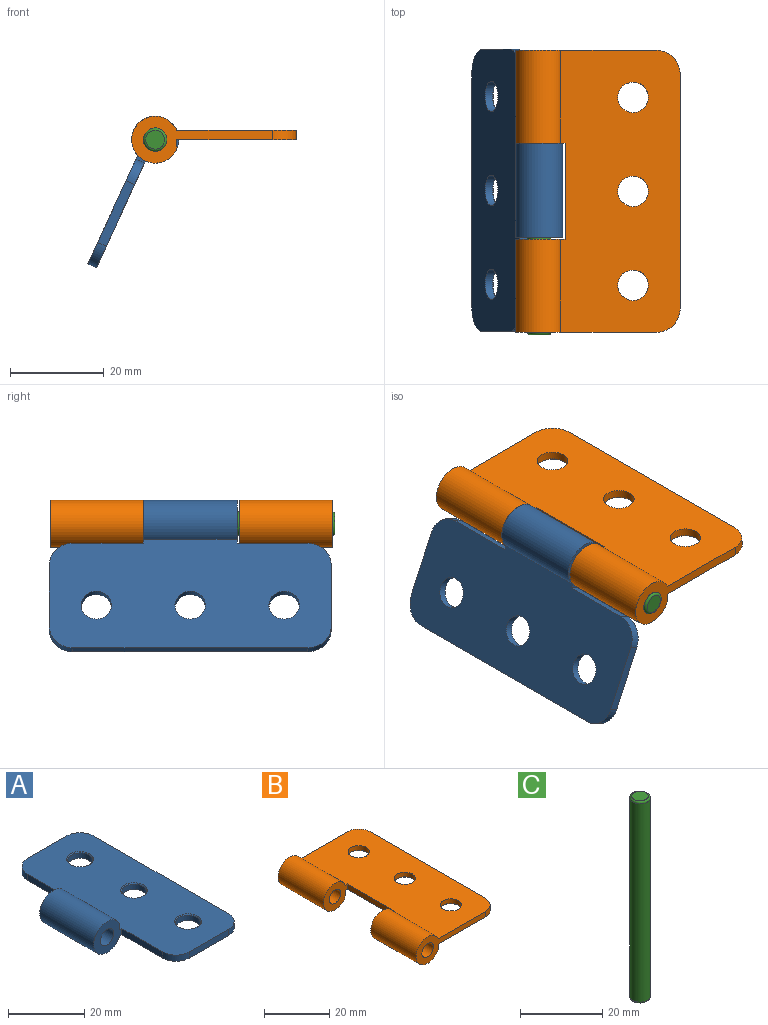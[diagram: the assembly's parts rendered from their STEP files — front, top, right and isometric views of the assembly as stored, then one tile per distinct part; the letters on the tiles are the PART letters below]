
ASSEMBLY  parts=3 mates=4
PART A: 22 faces, bbox 35x60x10 mm
  f0: cone r=3.5mm half-angle=45deg, axis (0,0,1), area 7.5mm2, adj f1,f10
  f1: cylinder r=3.25mm len=6.5mm, axis (0,0,1), area 35.7mm2, adj f0,f12
  f2: cone r=3.5mm half-angle=45deg, axis (0,0,1), area 7.5mm2, adj f3,f10
  f3: cylinder r=3.25mm len=6.5mm, axis (0,0,1), area 35.7mm2, adj f2,f12
  f4: cone r=3.5mm half-angle=45deg, axis (0,0,1), area 7.5mm2, adj f5,f10
  f5: cylinder r=3.25mm len=6.5mm, axis (0,0,1), area 35.7mm2, adj f4,f12
  f6: cylinder r=2.5mm len=20mm, axis (0,-1,0), area 314.2mm2, adj f16,f17
  f7: cylinder r=5mm len=20mm, axis (0,-1,0), area 546mm2, adj f12,f15,f16,f17
  f8: plane 15x2mm, normal (-1,0,0), area 30mm2, adj f10,f12,f17,f20
  f9: plane 15x2mm, normal (-1,0,0), area 30mm2, adj f10,f12,f16,f21
  f10: plane 60x25.42mm, normal (0,0,1), area 1351.4mm2, adj f0,f2,f4,f8,f9,f11,f13,f14
  f11: plane 50x2mm, normal (1,0,0), area 100mm2, adj f10,f12,f18,f19
  f12: plane 60x25.42mm, normal (0,0,-1), area 1367.3mm2, adj f1,f3,f5,f7,f8,f9,f11,f13
  f13: plane 14.5x2mm, normal (0,1,0), area 29mm2, adj f10,f12,f18,f21
  f14: plane 14.5x2mm, normal (0,-1,0), area 29mm2, adj f10,f12,f19,f20
  f15: plane 20x2mm, normal (1,0,0), area 40mm2, adj f7,f10,f16,f17
  f16: plane 10.5x10mm, normal (0,1,0), area 59.6mm2, adj f6,f7,f9,f10,f12,f15
  f17: plane 10.5x10mm, normal (0,-1,0), area 59.6mm2, adj f6,f7,f8,f10,f12,f15
  f18: cylinder r=5mm len=5mm, axis (0,0,1), area 15.7mm2, adj f10,f11,f12,f13
  f19: cylinder r=5mm len=5mm, axis (0,0,-1), area 15.7mm2, adj f10,f11,f12,f14
  f20: cylinder r=5mm len=5mm, axis (0,0,1), area 15.7mm2, adj f8,f10,f12,f14
  f21: cylinder r=5mm len=5mm, axis (0,0,-1), area 15.7mm2, adj f9,f10,f12,f13
PART B: 22 faces, bbox 35x60x10 mm
  f0: cone r=3.5mm half-angle=45deg, axis (0,0,-1), area 7.5mm2, adj f1,f10
  f1: cylinder r=3.25mm len=6.5mm, axis (0,0,-1), area 35.7mm2, adj f0,f12
  f2: cone r=3.5mm half-angle=45deg, axis (0,0,-1), area 7.5mm2, adj f3,f10
  f3: cylinder r=3.25mm len=6.5mm, axis (0,0,-1), area 35.7mm2, adj f2,f12
  f4: cone r=3.5mm half-angle=45deg, axis (0,0,-1), area 7.5mm2, adj f5,f10
  f5: cylinder r=3.25mm len=6.5mm, axis (0,0,-1), area 35.7mm2, adj f4,f12
  f6: cylinder r=2.5mm len=19.75mm, axis (0,-1,0), area 310.2mm2, adj f15,f19
  f7: cylinder r=5mm len=19.75mm, axis (0,-1,0), area 539.2mm2, adj f12,f13,f15,f19
  f8: cylinder r=2.5mm len=19.75mm, axis (0,-1,0), area 310.2mm2, adj f16,f18
  f9: cylinder r=5mm len=19.75mm, axis (0,-1,0), area 539.2mm2, adj f11,f12,f16,f18
  f10: plane 60x25.42mm, normal (0,0,-1), area 1380.1mm2, adj f0,f2,f4,f11,f13,f14,f15,f16
  f11: plane 19.75x2mm, normal (1,0,0), area 39.5mm2, adj f9,f10,f16,f18
  f12: plane 60x25.42mm, normal (0,0,1), area 1396mm2, adj f1,f3,f5,f7,f9,f14,f15,f16
  f13: plane 19.75x2mm, normal (1,0,0), area 39.5mm2, adj f7,f10,f15,f19
  f14: plane 50x2mm, normal (1,0,0), area 100mm2, adj f10,f12,f20,f21
  f15: plane 30x10mm, normal (0,1,0), area 98.6mm2, adj f6,f7,f10,f12,f13,f20
  f16: plane 30x10mm, normal (0,-1,0), area 98.6mm2, adj f8,f9,f10,f11,f12,f21
  f17: plane 20.5x2mm, normal (-1,0,0), area 41mm2, adj f10,f12,f18,f19
  f18: plane 10.5x10mm, normal (0,1,0), area 59.6mm2, adj f8,f9,f10,f11,f12,f17
  f19: plane 10.5x10mm, normal (0,-1,0), area 59.6mm2, adj f6,f7,f10,f12,f13,f17
  f20: cylinder r=5mm len=5mm, axis (0,0,1), area 15.7mm2, adj f10,f12,f14,f15
  f21: cylinder r=5mm len=5mm, axis (0,0,-1), area 15.7mm2, adj f10,f12,f14,f16
PART C: 5 faces, bbox 5.4x5.4x60 mm
  f0: torus R=2mm, axis (0,0,1), area 11.4mm2, adj f2,f3
  f1: torus R=2mm, axis (0,0,1), area 11.4mm2, adj f2,f4
  f2: cylinder r=2.5mm len=59mm, axis (0,0,-1), area 926.8mm2, adj f0,f1
  f3: plane 4x4mm, normal (0,0,1), area 12.6mm2, adj f0
  f4: plane 4x4mm, normal (0,0,-1), area 12.6mm2, adj f1
PLACE A rot(axis=(0,1,0),114.6deg) t=(-16.83,0,17.85)mm fixed
PLACE B t=(-16.83,-0.25,17.85)mm
PLACE C rot(axis=(1,0,0),90deg) t=(-16.83,29.25,17.85)mm
MATE planar B.f16 <-> C.f0  axis (0,-1,0) through (-12.24,-30.25,15.85)mm
MATE cylindrical C.f0 <-> A.f6  axis (0,1,0) through (-16.83,-0.75,17.85)mm
MATE cylindrical C.f0 <-> B.f6  axis (0,1,0) through (-16.83,-0.75,17.85)mm
MATE planar B.f19 <-> A.f16  axis (0,-1,0) through (-16.76,10,17.88)mm
